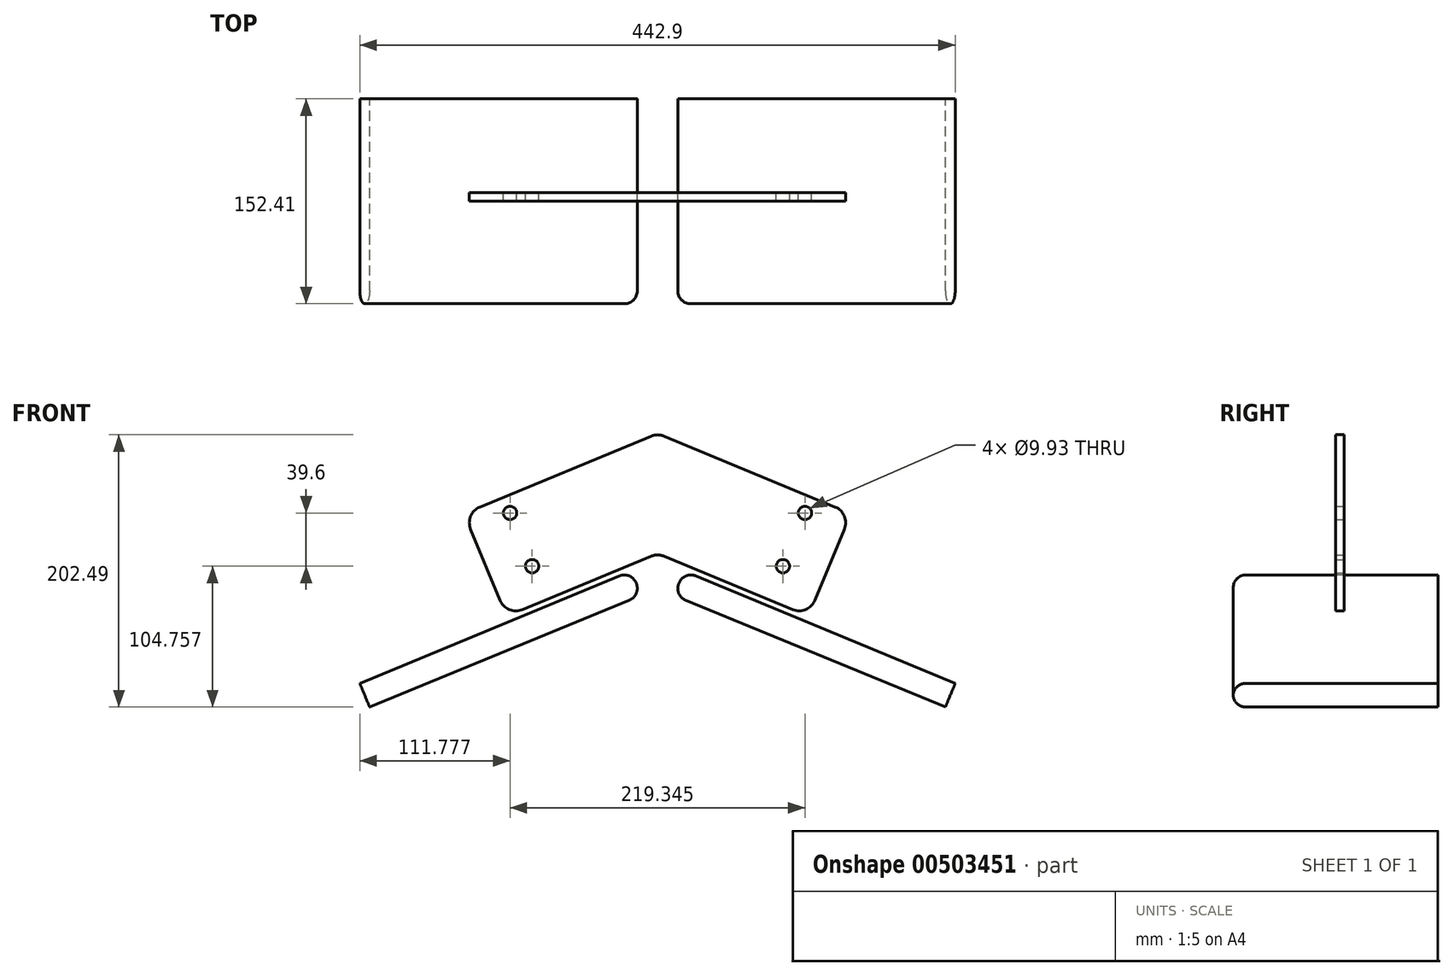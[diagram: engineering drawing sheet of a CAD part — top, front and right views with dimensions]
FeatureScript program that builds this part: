
annotation { "Feature Type Name" : "Feature", "Feature Type Description" : "" }
export const myFeature = defineFeature(function(context is Context, id is Id, definition is map)
    precondition{}
    {
        {
            var Q0;
            Q0=qCreatedBy(makeId("Front.planeOp"),FACE);
            var sketch = newSketch(context, id + "F0", { "sketchPlane" : qUnion([Q0])});
            skLineSegment(sketch, "E0", {"start": v(0, 0) * mm, "end": v(-112.28, -46.5) * mm});
            skLineSegment(sketch, "E1", {"start": v(0, 0) * mm, "end": v(0, 89.35) * mm});
            skLineSegment(sketch, "E2", {"start": v(-112.28, -46.5) * mm, "end": v(-143.87, 29.76) * mm});
            skLineSegment(sketch, "E3", {"start": v(-143.87, 29.76) * mm, "end": v(0, 89.35) * mm});
            skPoint(sketch, "E4", {"position": v(-15.88, -22.04) * mm});
            skLineSegment(sketch, "E5.MirrorCS", {"start": v(0, 0) * mm, "end": v(112.28, -46.5) * mm});
            skPoint(sketch, "E6.MirrorP", {"position": v(15.88, -22.04) * mm});
            skLineSegment(sketch, "E7.MirrorCS", {"start": v(112.28, -46.5) * mm, "end": v(143.87, 29.76) * mm});
            skLineSegment(sketch, "E8.MirrorCS", {"start": v(143.87, 29.76) * mm, "end": v(0, 89.35) * mm});
            skLineSegment(sketch, "E9", {"start": v(-15.88, -22.04) * mm, "end": v(-45.04, 48.36) * mm, "construction": true});
            skCircle(sketch, "E10", {"center": v(-93.27, -9.42) * mm, "radius": 4.97 * mm});
            skLineSegment(sketch, "E11", {"start": v(-93.27, -9.42) * mm, "end": v(-114.53, 41.91) * mm, "construction": true});
            skCircle(sketch, "E12", {"center": v(-109.67, 30.18) * mm, "radius": 4.97 * mm});
            skCircle(sketch, "E13.MirrorC", {"center": v(93.27, -9.42) * mm, "radius": 4.97 * mm});
            skCircle(sketch, "E14.MirrorC", {"center": v(109.67, 30.18) * mm, "radius": 4.97 * mm});
            skPoint(sketch, "E15", {"position": v(-103.9, 16.24) * mm});
            skLineSegment(sketch, "E16", {"start": v(-15.88, -22.04) * mm, "end": v(-19.63, -12.97) * mm});
            skLineSegment(sketch, "E17", {"start": v(-19.63, -12.97) * mm, "end": v(-221.45, -96.57) * mm});
            skLineSegment(sketch, "E18", {"start": v(-221.45, -96.57) * mm, "end": v(-217.8, -105.37) * mm});
            skLineSegment(sketch, "E19", {"start": v(-217.8, -105.37) * mm, "end": v(-15.88, -22.04) * mm, "construction": true});
            skLineSegment(sketch, "E20.MirrorCS", {"start": v(-214.19, -114.18) * mm, "end": v(-217.8, -105.37) * mm});
            skLineSegment(sketch, "E21.MirrorCS", {"start": v(-12.14, -31.12) * mm, "end": v(-214.19, -114.18) * mm});
            skLineSegment(sketch, "E22.MirrorCS", {"start": v(-15.87, -22.04) * mm, "end": v(-45.04, 48.36) * mm, "construction": true});
            skLineSegment(sketch, "E23", {"start": v(-19.63, -12.97) * mm, "end": v(-12.14, -31.12) * mm});
            skLineSegment(sketch, "E24.MirrorCS", {"start": v(19.63, -12.97) * mm, "end": v(12.14, -31.12) * mm});
            skLineSegment(sketch, "E25.MirrorCS", {"start": v(19.63, -12.97) * mm, "end": v(221.45, -96.57) * mm});
            skLineSegment(sketch, "E26.MirrorCS", {"start": v(12.14, -31.12) * mm, "end": v(214.19, -114.18) * mm});
            skLineSegment(sketch, "E27.MirrorCS", {"start": v(221.45, -96.57) * mm, "end": v(217.8, -105.37) * mm});
            skLineSegment(sketch, "E28.MirrorCS", {"start": v(214.19, -114.18) * mm, "end": v(217.8, -105.37) * mm});
            skSolve(sketch);
        }
        {
            var Q0;
            Q0=qSketchRegion(id+"F0",true);
            extrude(context, id + "F1", {"entities" : qUnion([Q0]), "depth" : 6.35 * mm, "offsetDistance" : 25.4 * mm, "symmetric" : true});
        }
        {
            var Q0;
            Q0=makeQuery(id+"F1.opExtrude","SWEPT_EDGE",EDGE,{"disambiguationData":[OSD([sQuery(id+"F0.wireOp",EDGE,"E2"),sQuery(id+"F0.wireOp",EDGE,"E3")])]});
            var Q1;
            Q1=makeQuery(id+"F1.opExtrude","SWEPT_EDGE",EDGE,{"disambiguationData":[OSD([sQuery(id+"F0.wireOp",EDGE,"E3"),sQuery(id+"F0.wireOp",EDGE,"E1"),sQuery(id+"F0.wireOp",EDGE,"E8.MirrorCS")])]});
            var Q2;
            Q2=makeQuery(id+"F1.opExtrude","SWEPT_EDGE",EDGE,{"disambiguationData":[OSD([sQuery(id+"F0.wireOp",EDGE,"E0"),sQuery(id+"F0.wireOp",EDGE,"E5.MirrorCS"),sQuery(id+"F0.wireOp",EDGE,"E1")])]});
            var Q3;
            Q3=makeQuery(id+"F1.opExtrude","SWEPT_EDGE",EDGE,{"disambiguationData":[OSD([sQuery(id+"F0.wireOp",EDGE,"E5.MirrorCS"),sQuery(id+"F0.wireOp",EDGE,"E7.MirrorCS")])]});
            var Q4;
            Q4=makeQuery(id+"F1.opExtrude","SWEPT_EDGE",EDGE,{"disambiguationData":[OSD([sQuery(id+"F0.wireOp",EDGE,"E7.MirrorCS"),sQuery(id+"F0.wireOp",EDGE,"E8.MirrorCS")])]});
            var Q5;
            Q5=makeQuery(id+"F1.opExtrude","SWEPT_EDGE",EDGE,{"disambiguationData":[OSD([sQuery(id+"F0.wireOp",EDGE,"E0"),sQuery(id+"F0.wireOp",EDGE,"E2")])]});
            fillet(context, id + "F2", {"entities" : qUnion([Q0, Q1, Q2, Q3, Q4, Q5]), "radius" : 12.7 * mm, "tangentPropagation" : true, "allowEdgeOverflow" : false});
        }
        {
            var Q0;
            Q0=makeQuery(id+"F1.opExtrude","CAP_FACE",FACE,{"disambiguationData":[OSD([sQuery(id+"F0.wireOp",EDGE,"E17"),sQuery(id+"F0.wireOp",EDGE,"E18"),sQuery(id+"F0.wireOp",EDGE,"E20.MirrorCS"),sQuery(id+"F0.wireOp",EDGE,"E21.MirrorCS"),sQuery(id+"F0.wireOp",EDGE,"E23")])],"isStart":false});
            var Q1;
            Q1=makeQuery(id+"F1.opExtrude","CAP_FACE",FACE,{"disambiguationData":[OSD([sQuery(id+"F0.wireOp",EDGE,"E24.MirrorCS"),sQuery(id+"F0.wireOp",EDGE,"E25.MirrorCS"),sQuery(id+"F0.wireOp",EDGE,"E26.MirrorCS"),sQuery(id+"F0.wireOp",EDGE,"E27.MirrorCS"),sQuery(id+"F0.wireOp",EDGE,"E28.MirrorCS")])],"isStart":false});
            extrude(context, id + "F3", {"entities" : qUnion([Q0, Q1]), "operationType" : NewBodyOperationType.ADD, "depth" : 152.4 * mm, "offsetDistance" : 25.4 * mm, "symmetric" : true});
        }
        {
            var Q0;
            Q0=makeQuery(id+"F3.opExtrude","SWEPT_EDGE",EDGE,{"disambiguationData":[OSD([sQuery(id+"F0.wireOp",EDGE,"E24.MirrorCS"),sQuery(id+"F0.wireOp",EDGE,"E25.MirrorCS")])]});
            var Q1;
            Q1=makeQuery(id+"F3.opExtrude","SWEPT_EDGE",EDGE,{"disambiguationData":[OSD([sQuery(id+"F0.wireOp",EDGE,"E24.MirrorCS"),sQuery(id+"F0.wireOp",EDGE,"E26.MirrorCS")])]});
            var Q2;
            Q2=makeQuery(id+"F3.opExtrude","CAP_EDGE",EDGE,{"disambiguationData":[OSD([sQuery(id+"F0.wireOp",EDGE,"E25.MirrorCS")])],"isStart":false});
            var Q3;
            Q3=makeQuery(id+"F3.opExtrude","CAP_EDGE",EDGE,{"disambiguationData":[OSD([sQuery(id+"F0.wireOp",EDGE,"E26.MirrorCS")])],"isStart":false});
            var Q4;
            Q4=makeQuery(id+"F3.opExtrude","SWEPT_EDGE",EDGE,{"disambiguationData":[OSD([sQuery(id+"F0.wireOp",EDGE,"E21.MirrorCS"),sQuery(id+"F0.wireOp",EDGE,"E23")])]});
            var Q5;
            Q5=makeQuery(id+"F3.opExtrude","CAP_EDGE",EDGE,{"disambiguationData":[OSD([sQuery(id+"F0.wireOp",EDGE,"E17")])],"isStart":false});
            var Q6;
            Q6=makeQuery(id+"F3.opExtrude","CAP_EDGE",EDGE,{"disambiguationData":[OSD([sQuery(id+"F0.wireOp",EDGE,"E21.MirrorCS")])],"isStart":false});
            var Q7;
            Q7=makeQuery(id+"F3.opExtrude","SWEPT_EDGE",EDGE,{"disambiguationData":[OSD([sQuery(id+"F0.wireOp",EDGE,"E17"),sQuery(id+"F0.wireOp",EDGE,"E23")])]});
            var Q8;
            Q8=makeQuery(id+"F3.opExtrude","CAP_EDGE",EDGE,{"disambiguationData":[OSD([sQuery(id+"F0.wireOp",EDGE,"E23")])],"isStart":false});
            var Q9;
            Q9=makeQuery(id+"F3.opExtrude","CAP_EDGE",EDGE,{"disambiguationData":[OSD([sQuery(id+"F0.wireOp",EDGE,"E24.MirrorCS")])],"isStart":false});
            fillet(context, id + "F4", {"entities" : qUnion([Q0, Q1, Q2, Q3, Q4, Q5, Q6, Q7, Q8, Q9]), "radius" : 9.52 * mm, "tangentPropagation" : true, "allowEdgeOverflow" : false});
        }
    });
